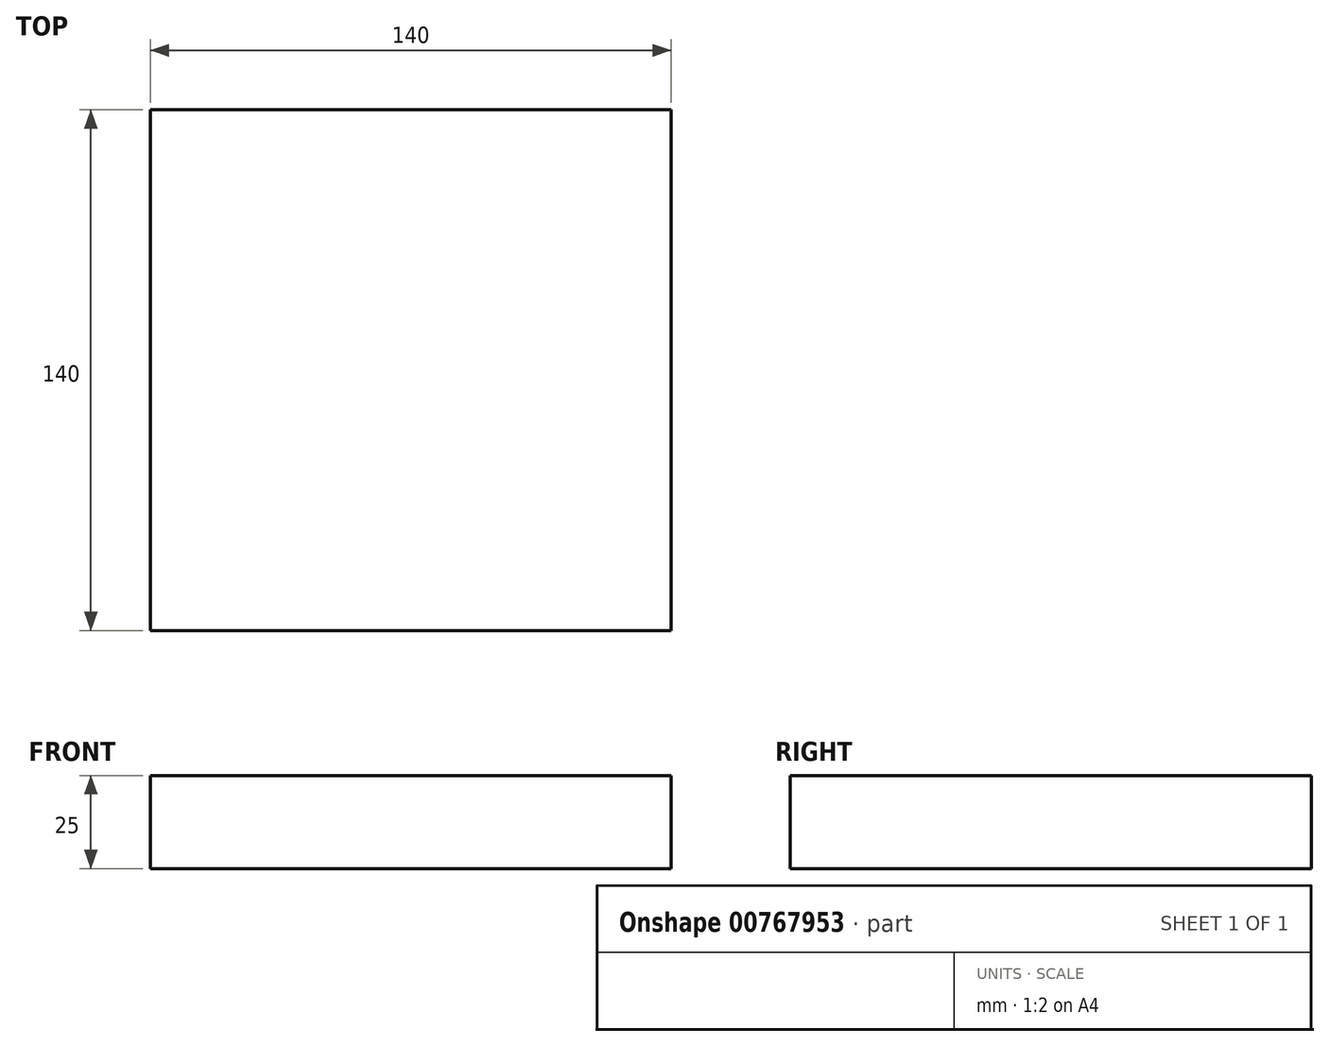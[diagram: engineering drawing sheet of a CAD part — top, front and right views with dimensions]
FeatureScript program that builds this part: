
annotation { "Feature Type Name" : "Feature", "Feature Type Description" : "" }
export const myFeature = defineFeature(function(context is Context, id is Id, definition is map)
    precondition{}
    {
        {
            var Q0;
            Q0=qCreatedBy(makeId("Top.planeOp"),FACE);
            var sketch = newSketch(context, id + "F0", { "sketchPlane" : qUnion([Q0])});
            skLineSegment(sketch, "E0.bottom", {"start": v(0, 0) * mm, "end": v(140, 0) * mm});
            skLineSegment(sketch, "E0.top", {"start": v(0, 140) * mm, "end": v(140, 140) * mm});
            skLineSegment(sketch, "E0.left", {"start": v(0, 0) * mm, "end": v(0, 140) * mm});
            skLineSegment(sketch, "E0.right", {"start": v(140, 0) * mm, "end": v(140, 140) * mm});
            skSolve(sketch);
        }
        {
            var Q0;
            Q0=makeQuery(id+"F0.imprint","IMPRINT",FACE,{"disambiguationData":[TD([[makeQuery(id+"F0.imprint","IMPRINT",EDGE,{"derivedFrom":sQuery(id+"F0.wireOp",EDGE,"E0.bottom")}),1.0]])]});
            extrude(context, id + "F1", {"entities" : qUnion([Q0]), "depth" : 25 * mm, "offsetDistance" : 25 * mm});
        }
    });
